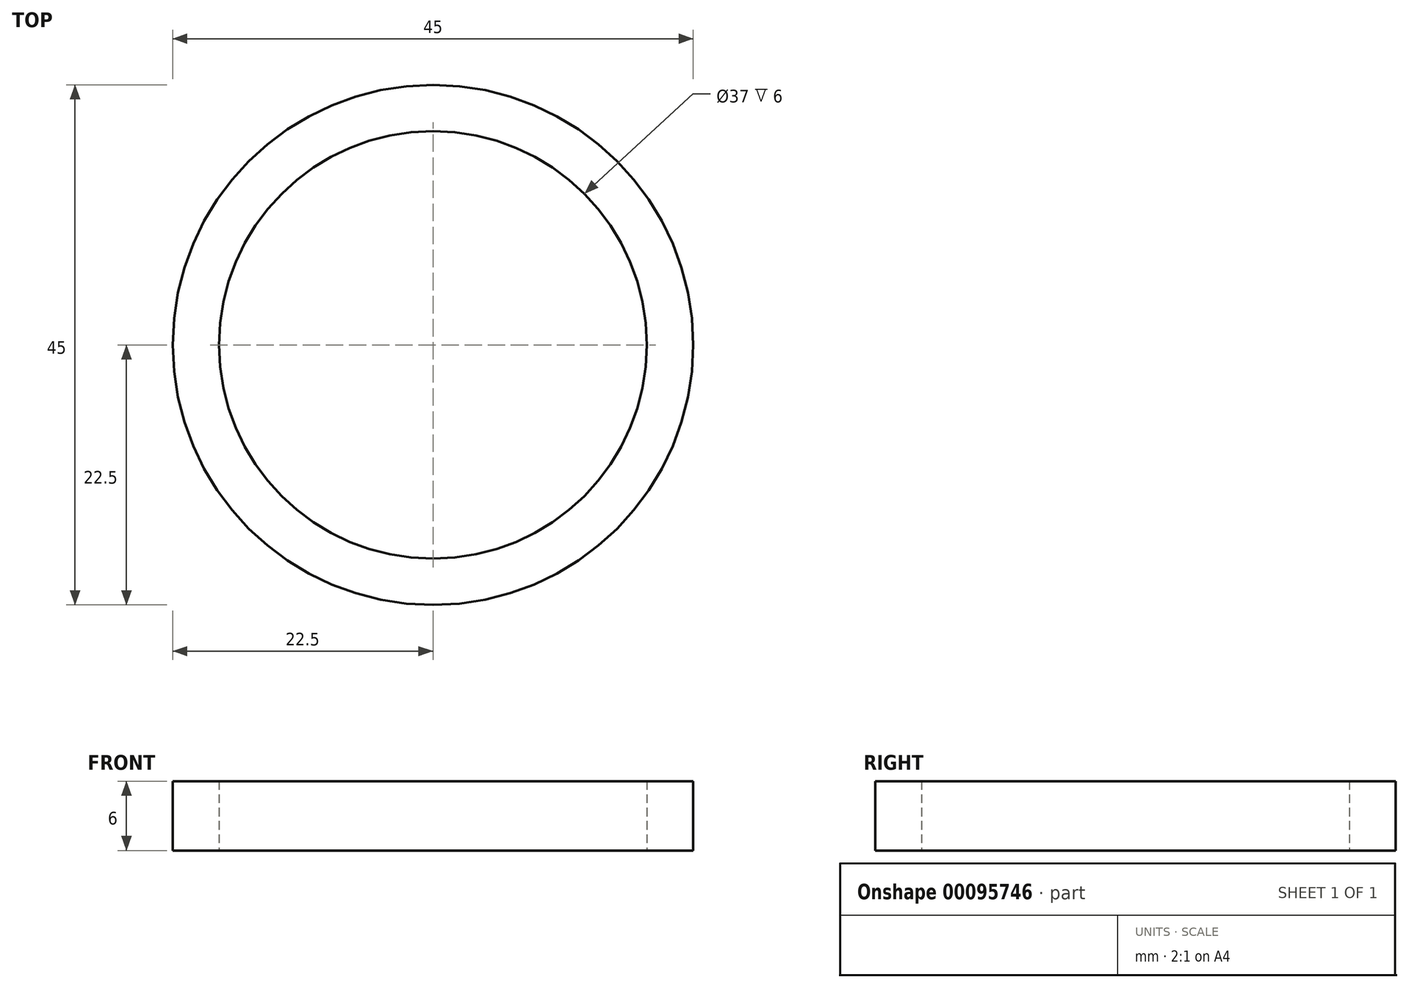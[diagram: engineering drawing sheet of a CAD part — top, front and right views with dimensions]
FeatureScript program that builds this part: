
annotation { "Feature Type Name" : "Feature", "Feature Type Description" : "" }
export const myFeature = defineFeature(function(context is Context, id is Id, definition is map)
    precondition{}
    {
        {
            var Q0;
            Q0=qCreatedBy(makeId("Top.planeOp"),FACE);
            var sketch = newSketch(context, id + "F0", { "sketchPlane" : qUnion([Q0])});
            skCircle(sketch, "E0", {"center": v(0, 0) * mm, "radius": 18.5 * mm});
            skCircle(sketch, "E1", {"center": v(0, 0) * mm, "radius": 22.5 * mm});
            skSolve(sketch);
        }
        {
            var Q0;
            Q0=makeQuery(id+"F0.imprint","IMPRINT",FACE,{"disambiguationData":[TD([[makeQuery(id+"F0.imprint","IMPRINT",EDGE,{"derivedFrom":sQuery(id+"F0.wireOp",EDGE,"E0")}),-1.0]])]});
            extrude(context, id + "F1", {"entities" : qUnion([Q0]), "depth" : 6 * mm});
        }
    });
